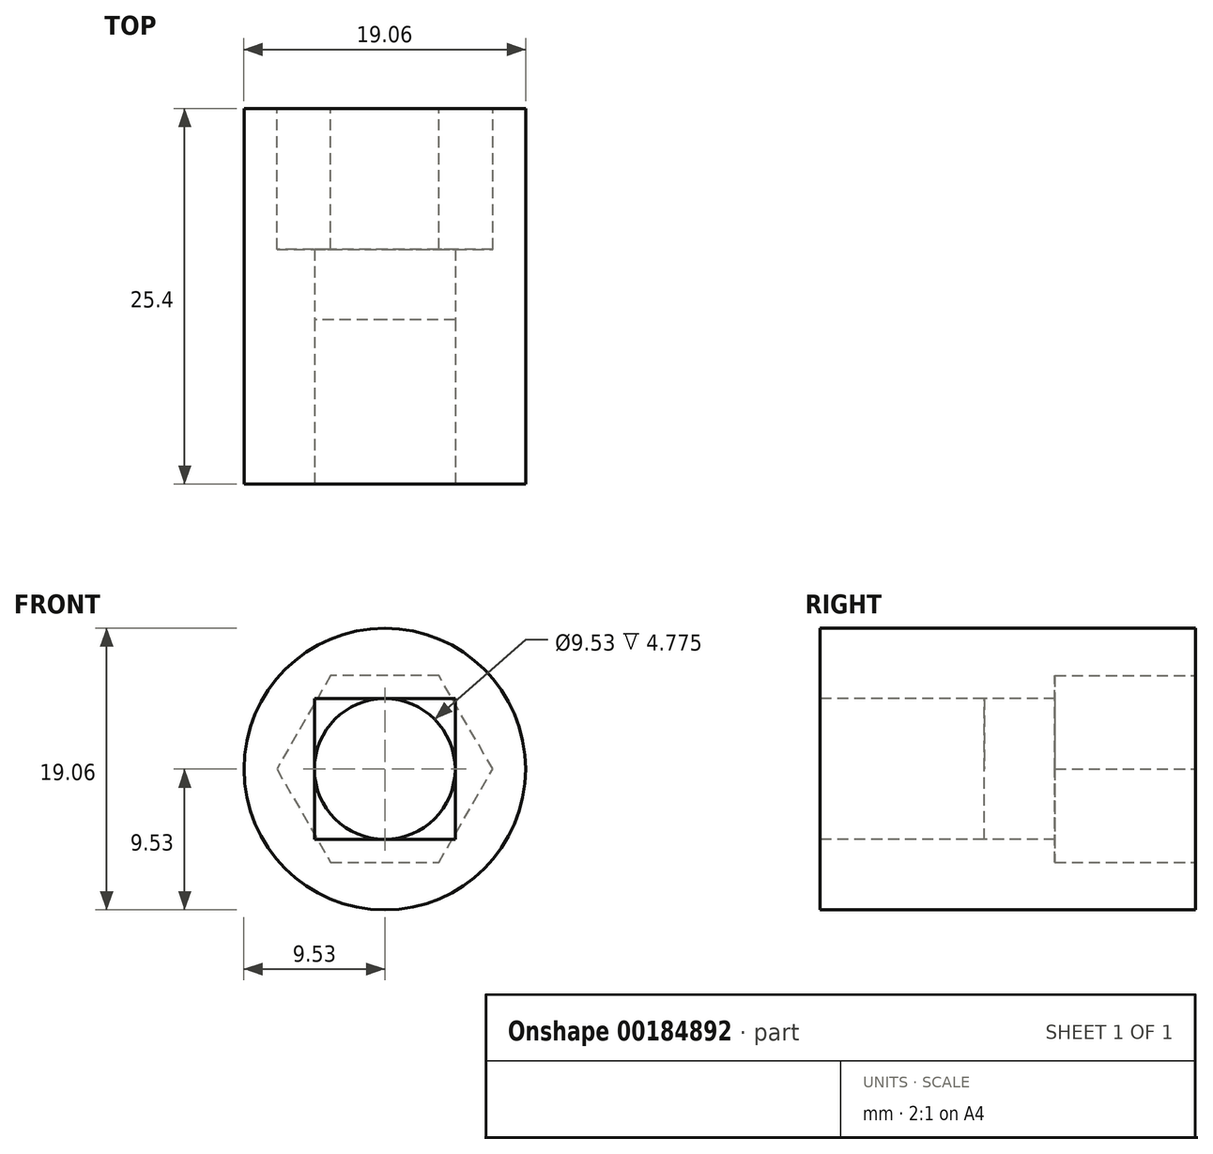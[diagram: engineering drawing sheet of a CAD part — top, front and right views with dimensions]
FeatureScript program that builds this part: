
annotation { "Feature Type Name" : "Feature", "Feature Type Description" : "" }
export const myFeature = defineFeature(function(context is Context, id is Id, definition is map)
    precondition{}
    {
        {
            var Q0;
            Q0=qCreatedBy(makeId("Front.planeOp"),FACE);
            var sketch = newSketch(context, id + "F0", { "sketchPlane" : qUnion([Q0])});
            skCircle(sketch, "E0", {"center": v(0, 0) * mm, "radius": 9.53 * mm});
            skSolve(sketch);
        }
        {
            var Q0;
            Q0 = qSketchRegion(id + "F0", true);
            extrude(context, id + "F1", {"entities" : qUnion([Q0]), "depth" : 25.4 * mm});
        }
        {
            var Q0;
            Q0=makeQuery(id+"F1.opExtrude","CAP_FACE",FACE,{"disambiguationData":[OSD([sQuery(id+"F0.wireOp",EDGE,"E0")])],"isStart":false});
            var sketch = newSketch(context, id + "F2", { "sketchPlane" : qUnion([Q0])});
            skLineSegment(sketch, "E1.bottom", {"start": v(4.76, -4.76) * mm, "end": v(-4.76, -4.76) * mm});
            skLineSegment(sketch, "E1.top", {"start": v(4.76, 4.76) * mm, "end": v(-4.76, 4.76) * mm});
            skLineSegment(sketch, "E1.left", {"start": v(4.76, -4.76) * mm, "end": v(4.76, 4.76) * mm});
            skLineSegment(sketch, "E1.right", {"start": v(-4.76, -4.76) * mm, "end": v(-4.76, 4.76) * mm});
            skPoint(sketch, "E1.middle", {"position": v(0, 0) * mm});
            skCircle(sketch, "E2", {"center": v(0, 0) * mm, "radius": 4.76 * mm});
            skSolve(sketch);
        }
        {
            var Q0;
            {var subQ0=sQuery(id+"F2.wireOp",EDGE,"E2");var subQ1=makeQuery(id+"F2.imprint","INTERSECT",VERTEX,{"derivedFrom":[sQuery(id+"F2.wireOp",EDGE,"E1.top"),subQ0]});Q0=makeQuery(id+"F2.imprint","IMPRINT",FACE,{"disambiguationData":[TD([[makeQuery(id+"F2.imprint","IMPRINT",EDGE,{"disambiguationData":[TD([[subQ1,1.0]])],"derivedFrom":subQ0}),1.0]])]});}
            extrude(context, id + "F3", {"entities" : qUnion([Q0]), "operationType" : NewBodyOperationType.REMOVE, "endBound" : BoundingType.THROUGH_ALL, "oppositeDirection" : true, "depth" : 25.4 * mm});
        }
        {
            var Q0;
            Q0 = qSketchRegion(id + "F2", true);
            extrude(context, id + "F4", {"entities" : qUnion([Q0]), "operationType" : NewBodyOperationType.REMOVE, "oppositeDirection" : true, "depth" : 11.1 * mm});
        }
        {
            var Q0;
            Q0=makeQuery(id+"F1.opExtrude","CAP_FACE",FACE,{"disambiguationData":[OSD([sQuery(id+"F0.wireOp",EDGE,"E0")])],"isStart":true});
            var sketch = newSketch(context, id + "F5", { "sketchPlane" : qUnion([Q0])});
            skCircle(sketch, "E3.cCircle", {"center": v(0, 0) * mm, "radius": 6.32 * mm, "construction": true});
            skLineSegment(sketch, "E3.0", {"start": v(3.65, 6.32) * mm, "end": v(7.3, 0) * mm});
            skLineSegment(sketch, "E3.1", {"start": v(7.3, 0) * mm, "end": v(3.65, -6.32) * mm});
            skLineSegment(sketch, "E3.2", {"start": v(3.65, -6.32) * mm, "end": v(-3.65, -6.32) * mm});
            skLineSegment(sketch, "E3.3", {"start": v(-3.65, -6.32) * mm, "end": v(-7.3, 0) * mm});
            skLineSegment(sketch, "E3.4", {"start": v(-7.3, 0) * mm, "end": v(-3.65, 6.32) * mm});
            skLineSegment(sketch, "E3.5", {"start": v(-3.65, 6.32) * mm, "end": v(3.65, 6.32) * mm});
            skPoint(sketch, "E3.0.midPoint", {"position": v(5.48, 3.16) * mm});
            skSolve(sketch);
        }
        {
            var Q0;
            Q0 = qSketchRegion(id + "F5", true);
            extrude(context, id + "F6", {"entities" : qUnion([Q0]), "operationType" : NewBodyOperationType.REMOVE, "oppositeDirection" : true, "depth" : 9.52 * mm});
        }
    });
